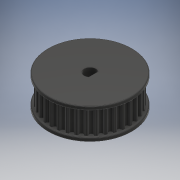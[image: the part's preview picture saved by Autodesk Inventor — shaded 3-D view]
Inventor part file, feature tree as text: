
AUTODESK INVENTOR PART (.ipt)
format: ipt  version: 2018 (Build 220112000, 112)  size: 446,976 bytes
history: native  units: mm
features: extrude x5, sketch x4, other x1, pattern_circular x1, fillet x1
ambient origin geometry x8: Origin, YZ Plane, XZ Plane, XY Plane, X Axis, Y Axis, Z Axis, Center Point
bodies: Solid1 (feature_tree)
feature tree (12):
  other  "Tooth"
  extrude  "Gear Solid Extrusion"  Depth=1.5mm
  extrude  "Tooth Cut-Out Extrusion"  Depth=0.85mm
  pattern_circular  "Teeth Array"  [2 undecoded]
  extrude  "Flange Extrusion Front"  TaperAngle=0.0deg  [1 undecoded]
  extrude  "Flange Extrusion Back"  Depth=10.0mm TaperAngle=0.0deg
  fillet  "Flange Fillet"  Radius=350.0mm
  extrude  "Extrusion5"  TaperAngle=360.0deg  [1 undecoded]
  sketch  "Sketch2"  dims[d2=16.711269mm d3=1.5mm]
  sketch  "Sketch3"  dims[d4=1.14mm d5=0.85mm]
  sketch  "Sketch4"  dims[d6=0.61mm]
  sketch  "Sketch5"  dims[d7=0.25mm d8=2.0mm d11=0.0mm d12=10.0mm d13=0.0mm d14=350.0mm d15=360.0deg d17=17.711269mm d19=0.0mm d20=17.711269mm d21=1.5mm d22=0.0mm d23=0.25mm d24=2.5mm d25=1.5mm d26=10.0mm d27=0.0mm]
note: 4 required parameter values undecoded (feature->parameter linkage not recoverable at this tier; creation-order binding heuristic only, values carry confidence <= 0.55)
